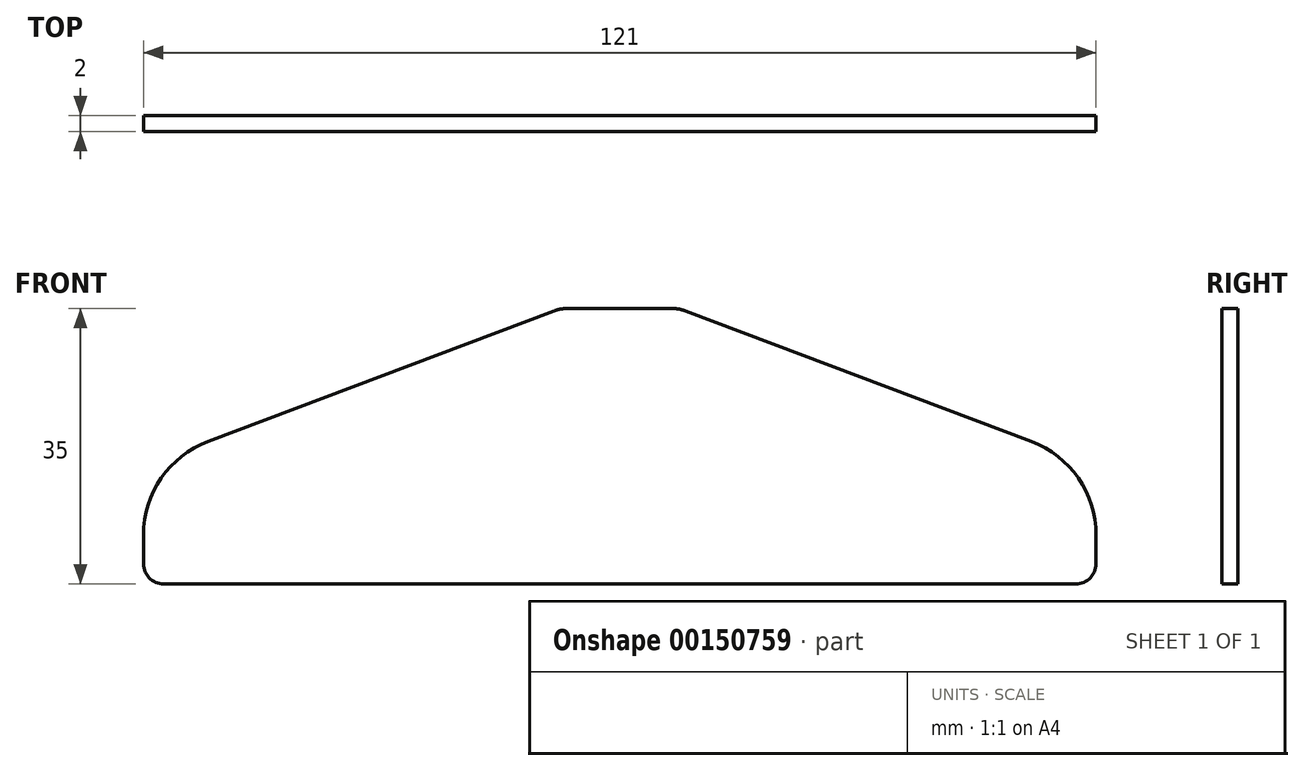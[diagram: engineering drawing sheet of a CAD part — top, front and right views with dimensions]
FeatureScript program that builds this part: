
annotation { "Feature Type Name" : "Feature", "Feature Type Description" : "" }
export const myFeature = defineFeature(function(context is Context, id is Id, definition is map)
    precondition{}
    {
        {
            var Q0;
            Q0=qCreatedBy(makeId("Front.planeOp"),FACE);
            var sketch = newSketch(context, id + "F0", { "sketchPlane" : qUnion([Q0])});
            skLineSegment(sketch, "E0", {"start": v(-60.5, 0) * mm, "end": v(60.5, 0) * mm});
            skLineSegment(sketch, "E1", {"start": v(-60.5, 0) * mm, "end": v(-60.5, 15) * mm});
            skLineSegment(sketch, "E2", {"start": v(-60.5, 15) * mm, "end": v(60.5, 15) * mm, "construction": true});
            skLineSegment(sketch, "E3", {"start": v(60.5, 0) * mm, "end": v(60.5, 15) * mm});
            skLineSegment(sketch, "E4", {"start": v(-7.5, 35) * mm, "end": v(7.5, 35) * mm});
            skLineSegment(sketch, "E5", {"start": v(-60.5, 15) * mm, "end": v(-7.5, 35) * mm});
            skLineSegment(sketch, "E6", {"start": v(7.5, 35) * mm, "end": v(60.5, 15) * mm});
            skSolve(sketch);
        }
        {
            var Q0;
            Q0=makeQuery(id+"F0.imprint","IMPRINT",FACE,{"disambiguationData":[TD([[makeQuery(id+"F0.imprint","IMPRINT",EDGE,{"derivedFrom":sQuery(id+"F0.wireOp",EDGE,"E0")}),1.0]])]});
            extrude(context, id + "F1", {"entities" : qUnion([Q0]), "depth" : 2 * mm});
        }
        {
            var Q0;
            Q0=makeQuery(id+"F1.opExtrude","SWEPT_EDGE",EDGE,{"disambiguationData":[OSD([sQuery(id+"F0.wireOp",EDGE,"E1"),sQuery(id+"F0.wireOp",EDGE,"E5")])]});
            var Q1;
            Q1=makeQuery(id+"F1.opExtrude","SWEPT_EDGE",EDGE,{"disambiguationData":[OSD([sQuery(id+"F0.wireOp",EDGE,"E3"),sQuery(id+"F0.wireOp",EDGE,"E6")])]});
            fillet(context, id + "F2", {"entities" : qUnion([Q0, Q1]), "radius" : 12.7 * mm, "tangentPropagation" : true, "allowEdgeOverflow" : false});
        }
        {
            var Q0;
            Q0=makeQuery(id+"F1.opExtrude","SWEPT_EDGE",EDGE,{"disambiguationData":[OSD([sQuery(id+"F0.wireOp",EDGE,"E0"),sQuery(id+"F0.wireOp",EDGE,"E1")])]});
            var Q1;
            Q1=makeQuery(id+"F1.opExtrude","SWEPT_EDGE",EDGE,{"disambiguationData":[OSD([sQuery(id+"F0.wireOp",EDGE,"E0"),sQuery(id+"F0.wireOp",EDGE,"E3")])]});
            fillet(context, id + "F3", {"entities" : qUnion([Q0, Q1]), "radius" : 2.54 * mm, "tangentPropagation" : true, "allowEdgeOverflow" : false});
        }
        {
            var Q0;
            Q0=makeQuery(id+"F1.opExtrude","SWEPT_EDGE",EDGE,{"disambiguationData":[OSD([sQuery(id+"F0.wireOp",EDGE,"E4"),sQuery(id+"F0.wireOp",EDGE,"E5")])]});
            var Q1;
            Q1=makeQuery(id+"F1.opExtrude","SWEPT_EDGE",EDGE,{"disambiguationData":[OSD([sQuery(id+"F0.wireOp",EDGE,"E4"),sQuery(id+"F0.wireOp",EDGE,"E6")])]});
            fillet(context, id + "F4", {"entities" : qUnion([Q0, Q1]), "radius" : 5.08 * mm, "tangentPropagation" : true, "allowEdgeOverflow" : false});
        }
    });
